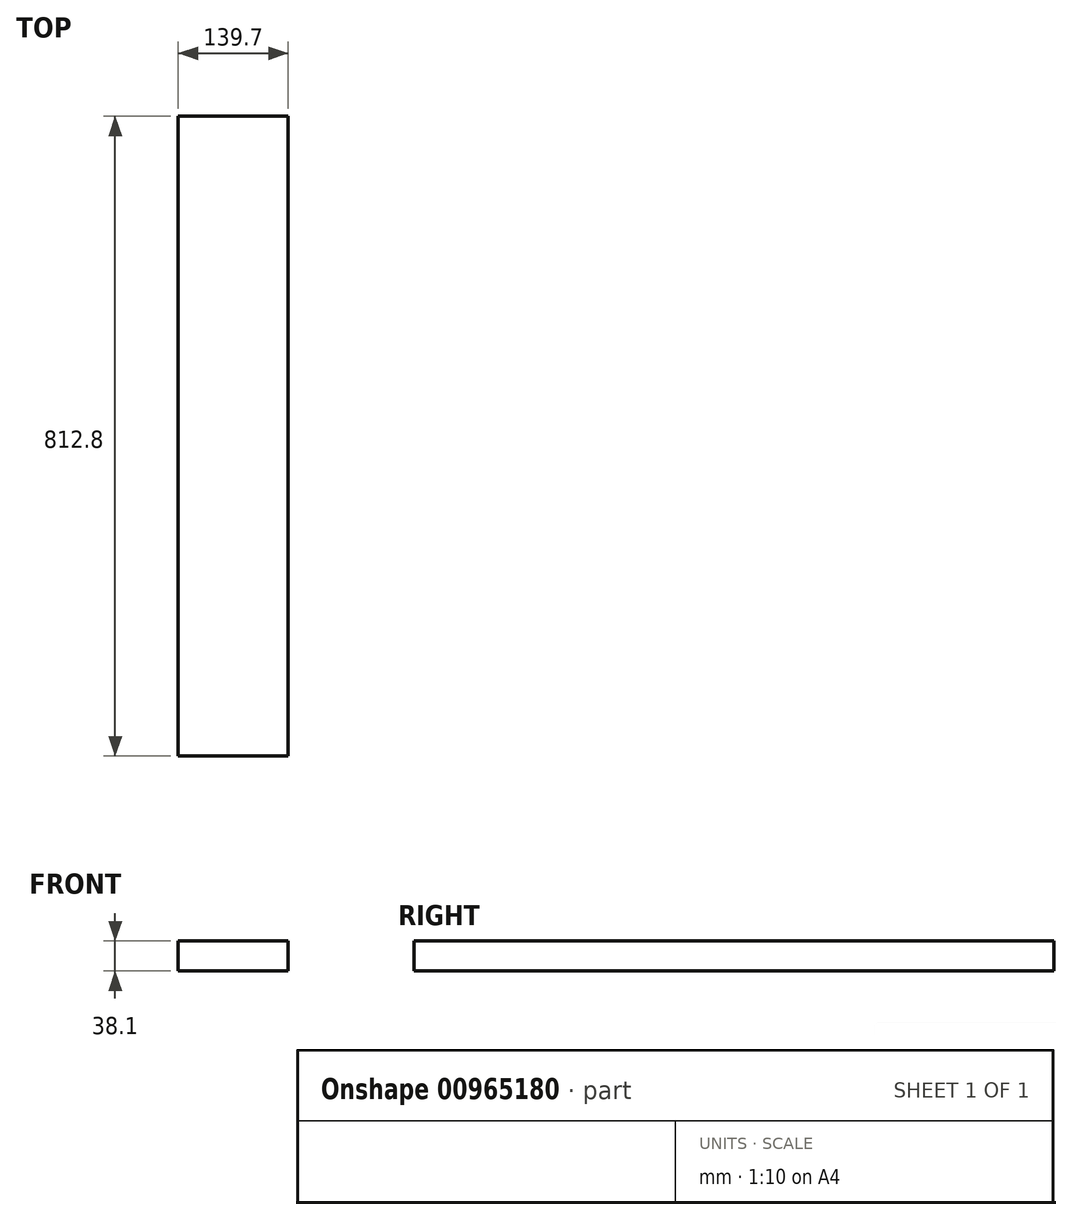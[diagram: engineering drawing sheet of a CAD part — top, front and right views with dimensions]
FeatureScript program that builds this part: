
annotation { "Feature Type Name" : "Feature", "Feature Type Description" : "" }
export const myFeature = defineFeature(function(context is Context, id is Id, definition is map)
    precondition{}
    {
        {
            var Q0;
            Q0=qCreatedBy(makeId("Front.planeOp"),FACE);
            var sketch = newSketch(context, id + "F0", { "sketchPlane" : qUnion([Q0])});
            skLineSegment(sketch, "E0.bottom", {"start": v(0, 0) * mm, "end": v(139.7, 0) * mm});
            skLineSegment(sketch, "E0.top", {"start": v(0, 38.1) * mm, "end": v(139.7, 38.1) * mm});
            skLineSegment(sketch, "E0.left", {"start": v(0, 0) * mm, "end": v(0, 38.1) * mm});
            skLineSegment(sketch, "E0.right", {"start": v(139.7, 0) * mm, "end": v(139.7, 38.1) * mm});
            skSolve(sketch);
        }
        {
            var Q0;
            Q0=makeQuery(id+"F0.imprint","IMPRINT",FACE,{"disambiguationData":[TD([[makeQuery(id+"F0.imprint","IMPRINT",EDGE,{"derivedFrom":sQuery(id+"F0.wireOp",EDGE,"E0.bottom")}),1.0]])]});
            extrude(context, id + "F1", {"entities" : qUnion([Q0]), "depth" : 812.8 * mm, "offsetDistance" : 25.4 * mm});
        }
    });
